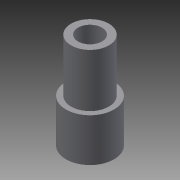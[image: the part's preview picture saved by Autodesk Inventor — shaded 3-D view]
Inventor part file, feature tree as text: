
AUTODESK INVENTOR PART (.ipt)
format: ipt  version: 2013 (Build 170138000, 138)  size: 81,408 bytes
history: native  units: in
note: dims shown in document units (in); Inventor stores cm internally (conversion verified against a paired STEP export)
features: extrude x2, sketch x2
ambient origin geometry x8: Origin, YZ Plane, XZ Plane, XY Plane, X Axis, Y Axis, Z Axis, Center Point
bodies: Solid1 (feature_tree)
feature tree (4):
  extrude  "Extrusion1"  Depth=0.25in
  extrude  "Extrusion2"  Depth=0.3937in
  sketch  "Sketch1"  dims[d0=0.5in d1=0.25in]
  sketch  "Sketch2"  dims[d2=1.0in d3=0.0in d4=0.3937in d5=0.5512in d6=0.0in]
